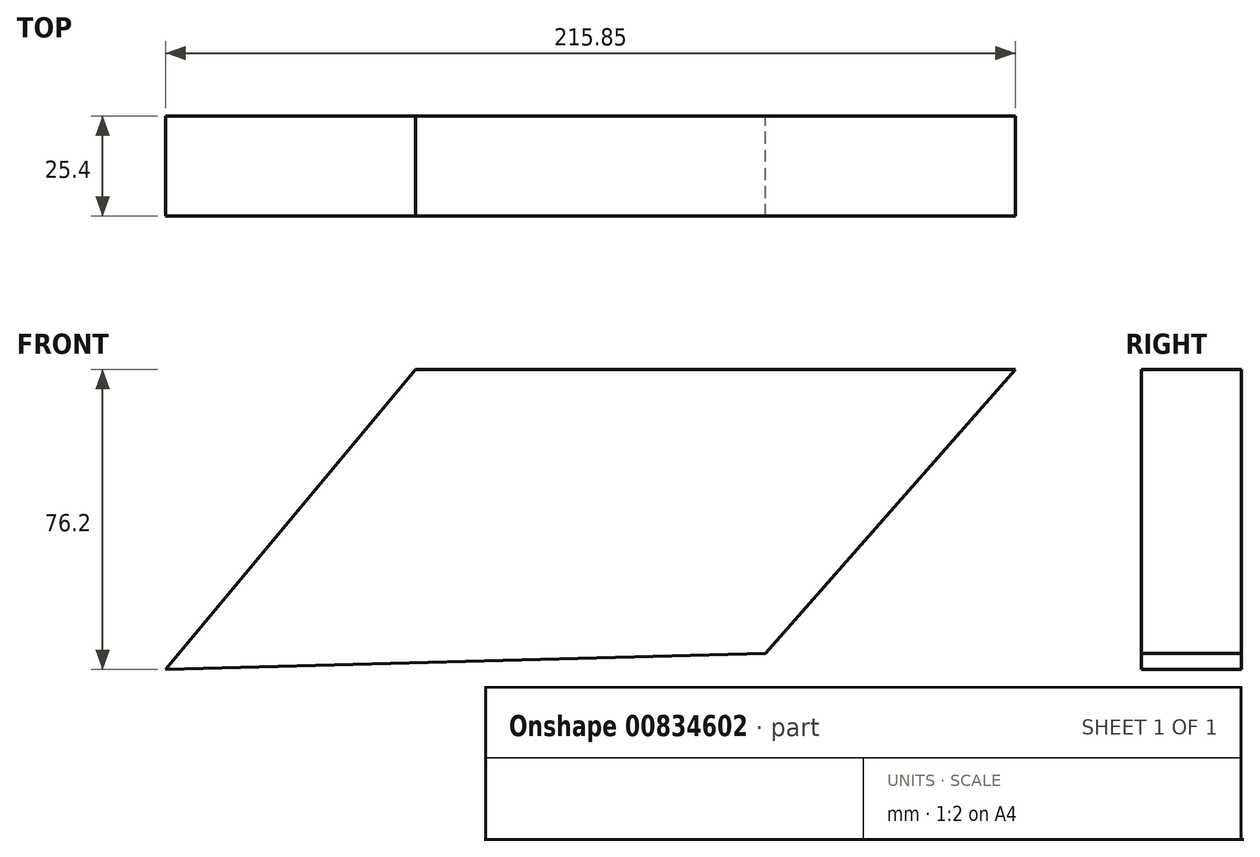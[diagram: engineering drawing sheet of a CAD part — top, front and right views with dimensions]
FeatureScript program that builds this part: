
annotation { "Feature Type Name" : "Feature", "Feature Type Description" : "" }
export const myFeature = defineFeature(function(context is Context, id is Id, definition is map)
    precondition{}
    {
        {
            var Q0;
            Q0=qCreatedBy(makeId("Front.planeOp"),FACE);
            var sketch = newSketch(context, id + "F0", { "sketchPlane" : qUnion([Q0])});
            skLineSegment(sketch, "E0", {"start": v(7.36, 0) * mm, "end": v(-144.99, -4.04) * mm});
            skLineSegment(sketch, "E1", {"start": v(-144.99, -4.04) * mm, "end": v(-81.49, 72.16) * mm});
            skLineSegment(sketch, "E2", {"start": v(-81.49, 72.16) * mm, "end": v(70.86, 72.16) * mm});
            skLineSegment(sketch, "E3", {"start": v(70.86, 72.16) * mm, "end": v(7.36, 0) * mm});
            skLineSegment(sketch, "E4", {"start": v(-81.49, 72.16) * mm, "end": v(-81.49, -2.35) * mm, "construction": true});
            skLineSegment(sketch, "E5", {"start": v(7.36, 0) * mm, "end": v(18.55, 72.16) * mm, "construction": true});
            skSolve(sketch);
        }
        {
            var Q0;
            Q0=makeQuery(id+"F0.imprint","IMPRINT",FACE,{"disambiguationData":[TD([[makeQuery(id+"F0.imprint","IMPRINT",EDGE,{"derivedFrom":sQuery(id+"F0.wireOp",EDGE,"E0")}),-1.0]])]});
            extrude(context, id + "F1", {"entities" : qUnion([Q0]), "depth" : 25.4 * mm, "offsetDistance" : 25.4 * mm});
        }
    });
